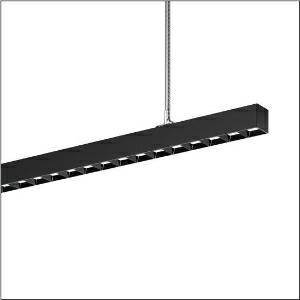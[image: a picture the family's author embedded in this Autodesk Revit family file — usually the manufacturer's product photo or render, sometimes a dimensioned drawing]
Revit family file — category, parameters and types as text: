
# Revit family: silica_21_51mx32dc3dbb
name_source: partatom
category: Lighting Fixtures
units: mm (PartAtom-declared; Revit-internal decimal feet)

## family parameters
Cut with Voids When Loaded = No
Host = Face
Light Source = No
Part Type = Normal
Room Calculation Point = No
Round Connector Dimension = Use Diameter
Shared = No

## types (1)
- --- (1 x LED, 18220 lm, 113 W, 3000K)
    Apparent Load = 113 VA
    CIE Flux Codes = 86 99 100 59 100
    Color Rendering = 80
    Color Temperature = 3000K
    Default Elevation = 1800 mm
    Description = Silica 21, office luminaire, primary light control with darklight reflector, of PMMA, black, CAT 2 (L<= 3000cd/m²), light emission: direct/indirect distribution, primary light characteristic: symmetric, installation type: suspended mounting, LED, rated luminous flux: 18.220lm, luminous efficacy: 161lm/W, light colour: 830, colour temperature: 3000K, control gear: DALI 2, with terminal, 3+2-pole, max. 2.5mm², mains connection: 220..240V, AC, 50/60Hz, rated input power: 113W, luminaire housing, of aluminium, matt jet black (RAL 9005), length: 3.004mm, width: 53mm, height: 53mm, protection rating (complete): IP20, insulation class (complete): insulation class I (protective earthing), certification: CE, permissible operating ambient temperature: 0..+35°C, standard: EN 50419, packaging unit: 1 piece
    Height = 53 mm
    Lamp = 1 x LED
    Lamp Light Flux = 18220 lm
    Lamp Power = 113 W
    Lamp count = 1
    Length = 3004 mm
    Luminous efficacy = 161 lm/W
    Manufacturer = Siteco
    ModVariant = No
    Model = 51MX32DC3DBB
    Mounting Place = Ceiling
    Mounting Type = Pendant
    Number of Poles = 1
    OnlyDefault = Yes
    Power Factor = 1
    Product Name = Silica 21
    Product group = office luminaire | ceiling pendant
    ProductGroupID = 903
    Protection Class = Protection class I
    Protection Degree = IP 20
    RLX_Detail_Level = 1
    RLX_Emergency_Light_Flux = 0 lm
    RLX_Emergency_Type = 0
    RLX_Emergency_Type_DB = No
    RlxData = <blob elided: 66725 chars, md5=3e41005f>
    Socket = socket
    Standby Power = 0 W
    System Light Flux = 18220 lm
    System Power = 113 W
    Type Comments = factory setting: luminous flux: 100 % | dim-lin: 254 | 391 mA
    Type Image = l_1335852.jpg
    URL = http://relux.com
    VarID = @adj_122235
    Voltage = 0 V
    Weight = 0.00 kg
    Width = 53 mm

## geometry (parser evidence)
native form markers: Blend x4, Sweep x11
no freeform markers — native parametric forms only
